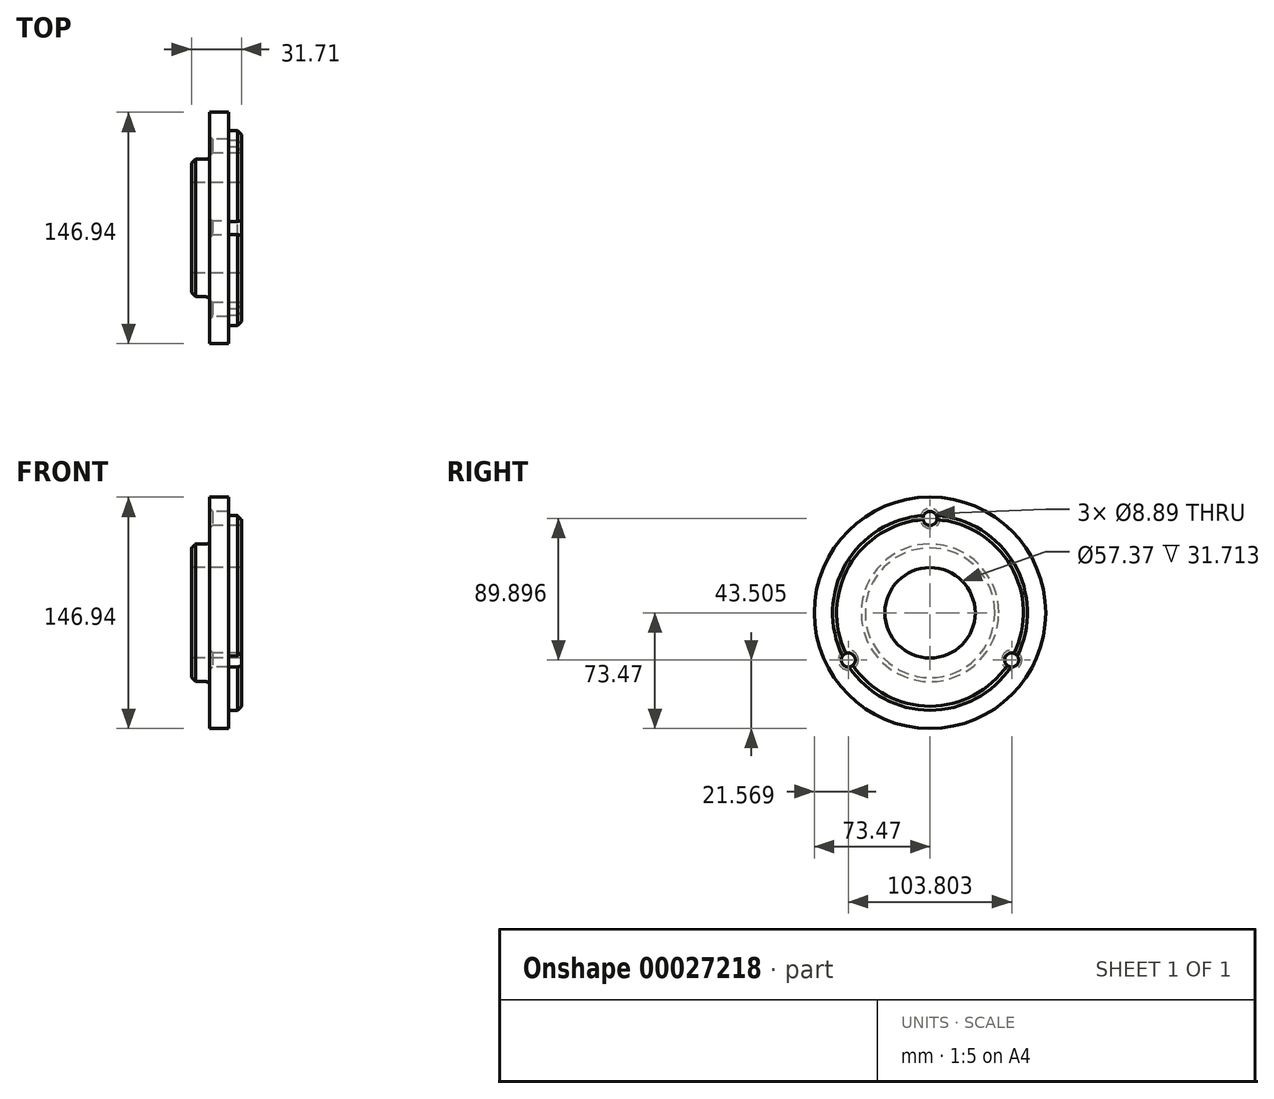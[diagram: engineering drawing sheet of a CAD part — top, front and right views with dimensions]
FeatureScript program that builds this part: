
annotation { "Feature Type Name" : "Feature", "Feature Type Description" : "" }
export const myFeature = defineFeature(function(context is Context, id is Id, definition is map)
    precondition{}
    {
        {
            var Q0;
            Q0=qCreatedBy(makeId("Front.planeOp"),FACE);
            var sketch = newSketch(context, id + "F0", { "sketchPlane" : qUnion([Q0])});
            skLineSegment(sketch, "E0", {"start": v(0, 28.69) * mm, "end": v(0, 43.7) * mm});
            skLineSegment(sketch, "E1", {"start": v(0, 43.7) * mm, "end": v(11.62, 43.7) * mm});
            skLineSegment(sketch, "E2", {"start": v(11.62, 43.7) * mm, "end": v(11.62, 73.47) * mm});
            skLineSegment(sketch, "E3", {"start": v(11.62, 73.47) * mm, "end": v(23.48, 73.47) * mm});
            skLineSegment(sketch, "E4", {"start": v(23.48, 73.47) * mm, "end": v(23.48, 61.85) * mm});
            skLineSegment(sketch, "E5", {"start": v(23.48, 61.85) * mm, "end": v(31.71, 61.85) * mm});
            skLineSegment(sketch, "E6", {"start": v(31.71, 61.85) * mm, "end": v(31.71, 28.69) * mm});
            skLineSegment(sketch, "E7", {"start": v(31.71, 28.69) * mm, "end": v(0, 28.69) * mm});
            skLineSegment(sketch, "E8", {"start": v(0, 0) * mm, "end": v(32.99, 0) * mm, "construction": true});
            skSolve(sketch);
        }
        {
            var Q0;
            Q0=makeQuery(id+"F0.imprint","IMPRINT",FACE,{"disambiguationData":[TD([[makeQuery(id+"F0.imprint","IMPRINT",EDGE,{"derivedFrom":sQuery(id+"F0.wireOp",EDGE,"E0")}),-1.0]])]});
            var Q1;
            Q1=sQuery(id+"F0.wireOp",EDGE,"E8");
            revolve(context, id + "F1", {"entities" : qUnion([Q0]), "axis" : qUnion([Q1]), "revolveType" : RevolveType.FULL});
        }
        {
            var Q0;
            Q0=makeQuery(id+"F1.opRevolve","SWEPT_EDGE",EDGE,{"disambiguationData":[OSD([sQuery(id+"F0.wireOp",EDGE,"E0"),sQuery(id+"F0.wireOp",EDGE,"E1")])]});
            chamfer(context, id + "F2", {"entities" : qUnion([Q0]), "width" : 2.54 * mm, "tangentPropagation" : true});
        }
        {
            var Q0;
            Q0=makeQuery(id+"F1.opRevolve","SWEPT_EDGE",EDGE,{"disambiguationData":[OSD([sQuery(id+"F0.wireOp",EDGE,"E1"),sQuery(id+"F0.wireOp",EDGE,"E2")])]});
            fillet(context, id + "F3", {"entities" : qUnion([Q0]), "radius" : 2.54 * mm, "tangentPropagation" : true, "allowEdgeOverflow" : false});
        }
        {
            var Q0;
            Q0=makeQuery(id+"F1.opRevolve","SWEPT_EDGE",EDGE,{"disambiguationData":[OSD([sQuery(id+"F0.wireOp",EDGE,"E5"),sQuery(id+"F0.wireOp",EDGE,"E6")])]});
            chamfer(context, id + "F4", {"entities" : qUnion([Q0]), "width" : 2.54 * mm, "tangentPropagation" : true});
        }
        {
            var Q0;
            Q0=makeQuery(id+"F1.opRevolve","SWEPT_FACE",FACE,{"disambiguationData":[OSD([sQuery(id+"F0.wireOp",EDGE,"E2")])]});
            var sketch = newSketch(context, id + "F5", { "sketchPlane" : qUnion([Q0])});
            skCircle(sketch, "E9", {"center": v(0, 59.93) * mm, "radius": 7.04 * mm});
            skCircle(sketch, "E10.1.0", {"center": v(-51.9, -29.97) * mm, "radius": 7.04 * mm});
            skCircle(sketch, "E10.2.0", {"center": v(51.9, -29.97) * mm, "radius": 7.04 * mm});
            skPoint(sketch, "E10.center", {"position": v(0, 0) * mm});
            skSolve(sketch);
        }
        {
            var Q0;
            Q0=sQuery(id+"F5.wireOp",VERTEX,"E9.center");
            var Q1;
            Q1=sQuery(id+"F5.wireOp",VERTEX,"E10.1.0.center");
            var Q2;
            Q2=sQuery(id+"F5.wireOp",VERTEX,"E10.2.0.center");
            var Q3;
            Q3=makeQuery(id+"F1.opRevolve","SWEPT_BODY",BODY,{"disambiguationData":[OSD([sQuery(id+"F0.wireOp",EDGE,"E0"),sQuery(id+"F0.wireOp",EDGE,"E1"),sQuery(id+"F0.wireOp",EDGE,"E2"),sQuery(id+"F0.wireOp",EDGE,"E3"),sQuery(id+"F0.wireOp",EDGE,"E4"),sQuery(id+"F0.wireOp",EDGE,"E5"),sQuery(id+"F0.wireOp",EDGE,"E6"),sQuery(id+"F0.wireOp",EDGE,"E7")])]});
            hole(context, id + "F6", {"style" : HoleStyle.C_SINK, "holeDiameter" : 8.9 * mm, "cSinkDiameter" : 12.7 * mm, "endStyle" : HoleEndStyle.THROUGH, "locations" : qUnion([Q0, Q1, Q2]), "scope" : qUnion([Q3]), "cSinkAngle" : 90 * degree});
        }
    });
